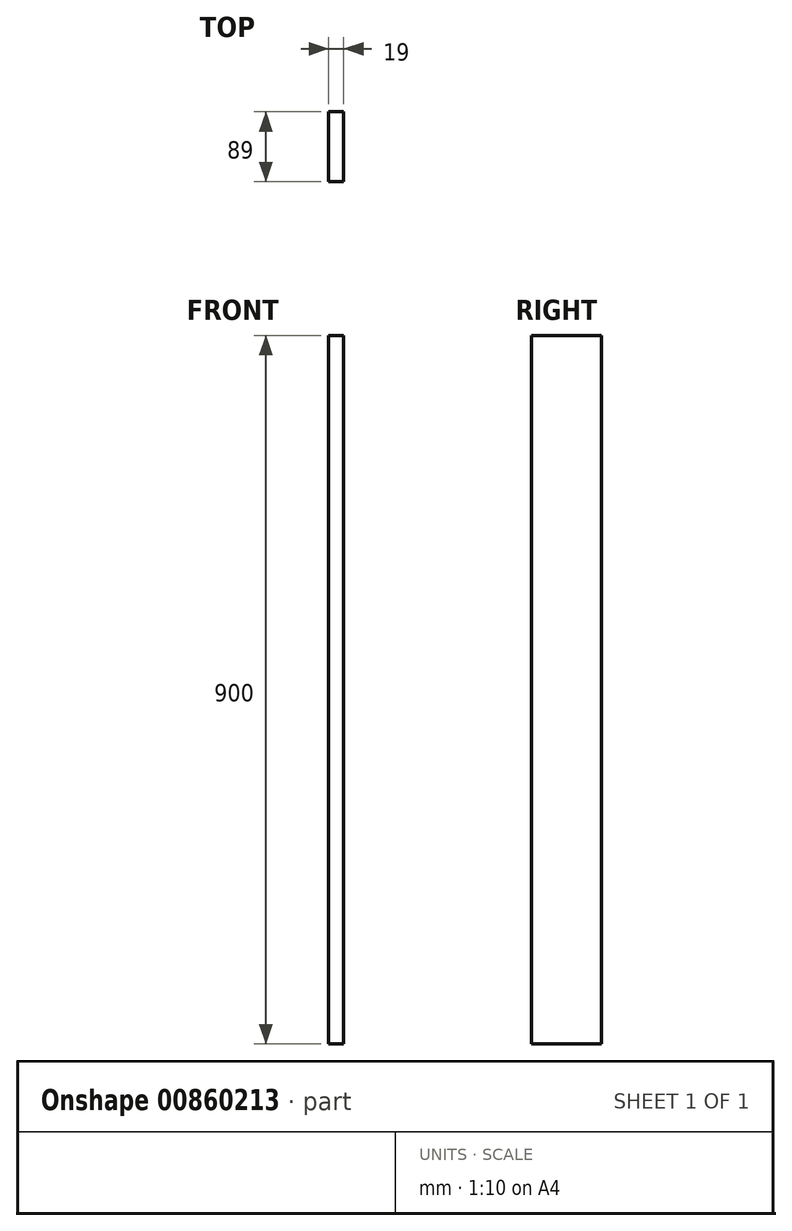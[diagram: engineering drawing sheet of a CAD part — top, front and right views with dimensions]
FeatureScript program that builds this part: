
annotation { "Feature Type Name" : "Feature", "Feature Type Description" : "" }
export const myFeature = defineFeature(function(context is Context, id is Id, definition is map)
    precondition{}
    {
        {
            var Q0;
            Q0=qCreatedBy(makeId("Top.planeOp"),FACE);
            var sketch = newSketch(context, id + "F0", { "sketchPlane" : qUnion([Q0])});
            skLineSegment(sketch, "E0.bottom", {"start": v(0, 0) * mm, "end": v(-19, 0) * mm});
            skLineSegment(sketch, "E0.top", {"start": v(0, 89) * mm, "end": v(-19, 89) * mm});
            skLineSegment(sketch, "E0.left", {"start": v(0, 0) * mm, "end": v(0, 89) * mm});
            skLineSegment(sketch, "E0.right", {"start": v(-19, 0) * mm, "end": v(-19, 89) * mm});
            skSolve(sketch);
        }
        {
            var Q0;
            Q0=makeQuery(id+"F0.imprint","IMPRINT",FACE,{"disambiguationData":[TD([[makeQuery(id+"F0.imprint","IMPRINT",EDGE,{"derivedFrom":sQuery(id+"F0.wireOp",EDGE,"E0.bottom")}),-1.0]])]});
            extrude(context, id + "F1", {"entities" : qUnion([Q0]), "depth" : 900 * mm, "offsetDistance" : 25 * mm});
        }
    });
